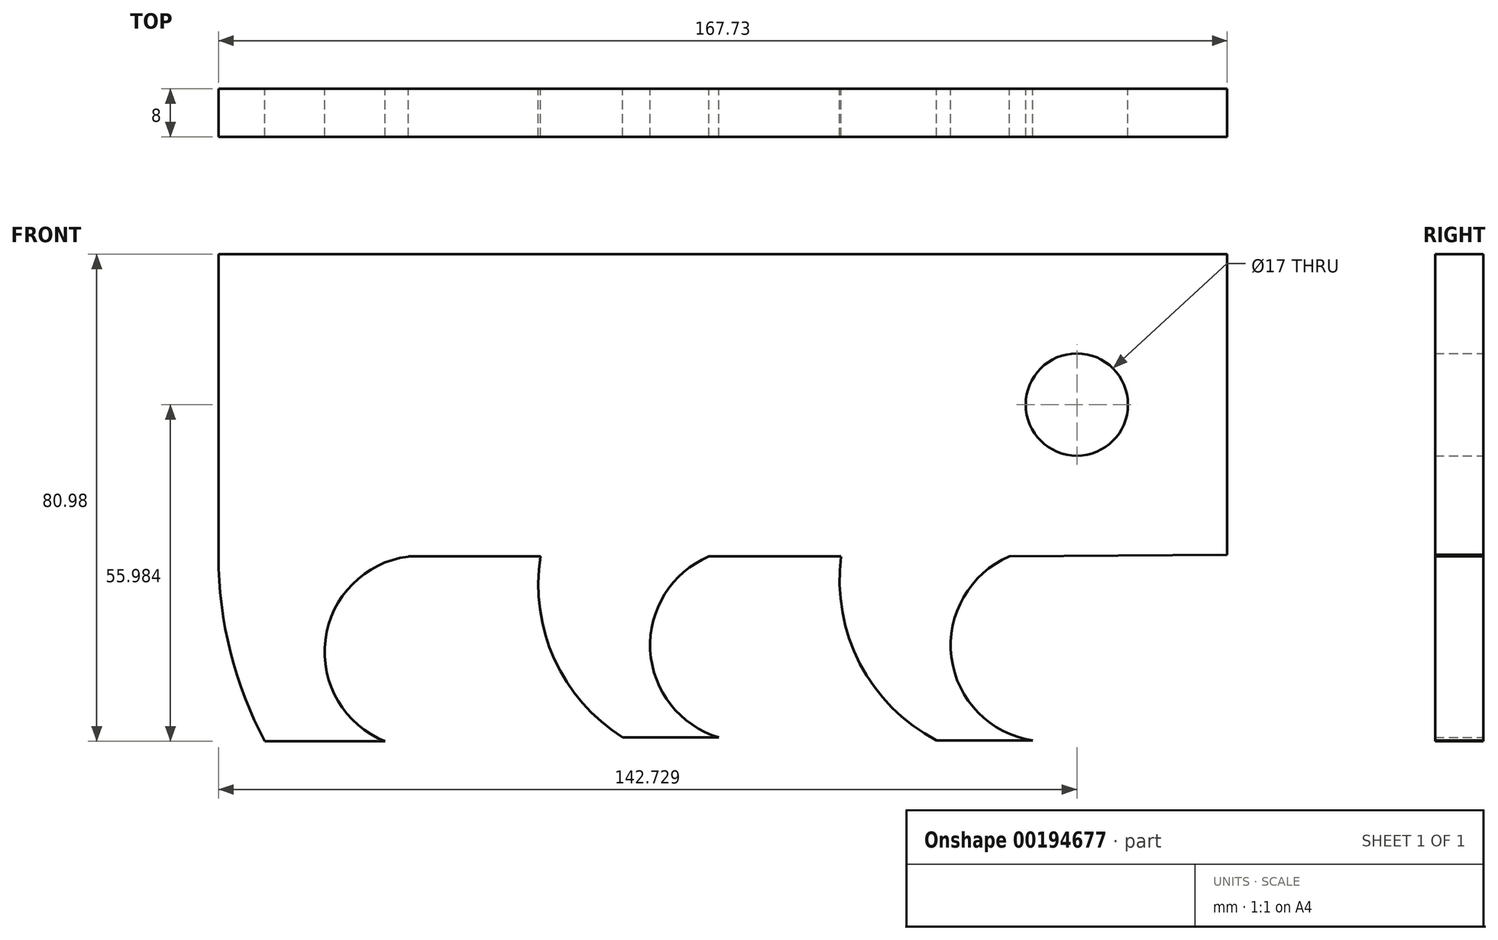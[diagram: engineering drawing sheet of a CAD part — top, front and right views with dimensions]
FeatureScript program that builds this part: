
annotation { "Feature Type Name" : "Feature", "Feature Type Description" : "" }
export const myFeature = defineFeature(function(context is Context, id is Id, definition is map)
    precondition{}
    {
        {
            var Q0;
            Q0=qCreatedBy(makeId("Front.planeOp"),FACE);
            var sketch = newSketch(context, id + "F0", { "sketchPlane" : qUnion([Q0])});
            skLineSegment(sketch, "E0", {"start": v(-79.72, 80.98) * mm, "end": v(88, 80.98) * mm});
            skLineSegment(sketch, "E1", {"start": v(88, 80.98) * mm, "end": v(88, 30.98) * mm});
            skLineSegment(sketch, "E2", {"start": v(23.82, 30.73) * mm, "end": v(1.82, 30.73) * mm});
            skArc(sketch, "E3", {"start": v(51.82, 30.73) * mm, "mid": v(42.15, 13.98) * mm, "end": v(55.68, 0.16) * mm});
            skArc(sketch, "E4", {"start": v(1.82, 30.73) * mm, "mid": v(-7.93, 15.12) * mm, "end": v(3.46, 0.66) * mm});
            skLineSegment(sketch, "E5", {"start": v(-26.18, 30.73) * mm, "end": v(-48.18, 30.73) * mm});
            skLineSegment(sketch, "E6", {"start": v(-72, 0) * mm, "end": v(-52, 0) * mm});
            skArc(sketch, "E7", {"start": v(-48.18, 30.73) * mm, "mid": v(-61.96, 16.84) * mm, "end": v(-52, 0) * mm});
            skLineSegment(sketch, "E8", {"start": v(-79.72, 80.98) * mm, "end": v(-79.72, 30.73) * mm});
            skCircle(sketch, "E9", {"center": v(63, 55.98) * mm, "radius": 8.5 * mm});
            skLineSegment(sketch, "E10", {"start": v(88, 30.98) * mm, "end": v(51.82, 30.73) * mm});
            skLineSegment(sketch, "E11", {"start": v(55.68, 0.16) * mm, "end": v(39.68, 0.16) * mm});
            skLineSegment(sketch, "E12", {"start": v(3.46, 0.66) * mm, "end": v(-12.54, 0.66) * mm});
            skArc(sketch, "E13", {"start": v(23.82, 30.73) * mm, "mid": v(26.92, 12.94) * mm, "end": v(39.68, 0.16) * mm});
            skArc(sketch, "E14", {"start": v(-26.18, 30.73) * mm, "mid": v(-23.87, 13.65) * mm, "end": v(-12.54, 0.66) * mm});
            skArc(sketch, "E15", {"start": v(-79.72, 30.73) * mm, "mid": v(-77.76, 14.89) * mm, "end": v(-72, 0) * mm});
            skSolve(sketch);
        }
        {
            var Q0;
            Q0=makeQuery(id+"F0.imprint","IMPRINT",FACE,{"disambiguationData":[TD([[makeQuery(id+"F0.imprint","IMPRINT",EDGE,{"derivedFrom":sQuery(id+"F0.wireOp",EDGE,"E0")}),-1.0]])]});
            extrude(context, id + "F1", {"entities" : qUnion([Q0]), "depth" : 8 * mm, "offsetDistance" : 25 * mm});
        }
    });
